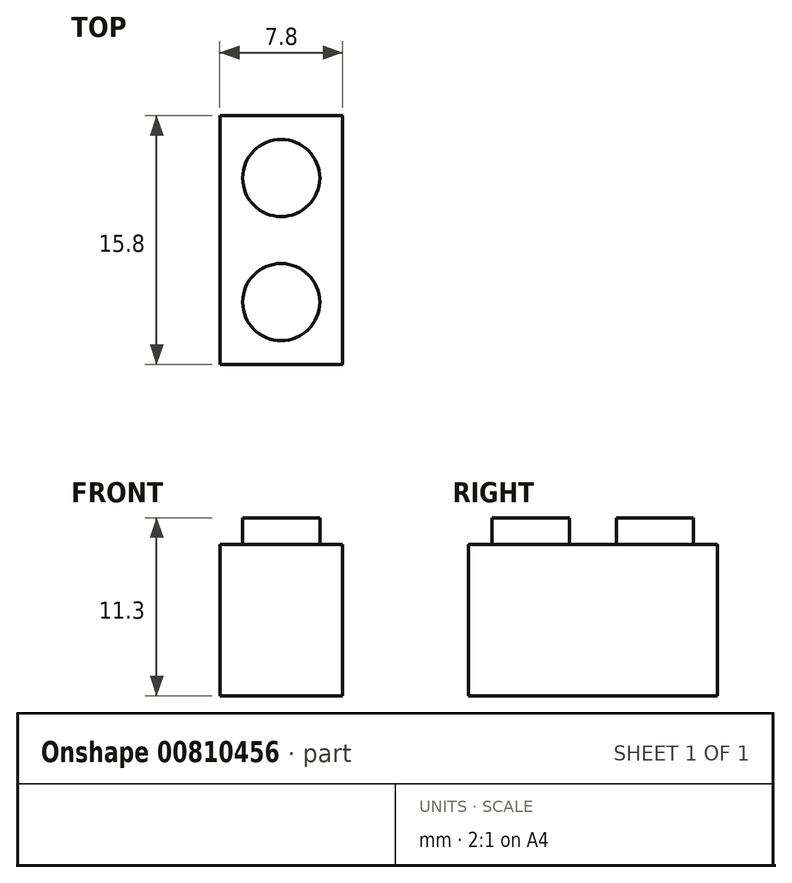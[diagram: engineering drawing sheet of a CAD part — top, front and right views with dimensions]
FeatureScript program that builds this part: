
annotation { "Feature Type Name" : "Feature", "Feature Type Description" : "" }
export const myFeature = defineFeature(function(context is Context, id is Id, definition is map)
    precondition{}
    {
        {
            var Q0;
            Q0=qCreatedBy(makeId("Top.planeOp"),FACE);
            var sketch = newSketch(context, id + "F0", { "sketchPlane" : qUnion([Q0])});
            skLineSegment(sketch, "E0", {"start": v(-4.58, 12.27) * mm, "end": v(-4.58, -3.53) * mm});
            skLineSegment(sketch, "E1", {"start": v(-4.58, -3.53) * mm, "end": v(3.22, -3.53) * mm});
            skLineSegment(sketch, "E2", {"start": v(3.22, -3.53) * mm, "end": v(3.22, 12.27) * mm});
            skLineSegment(sketch, "E3", {"start": v(3.22, 12.27) * mm, "end": v(-4.58, 12.27) * mm});
            skSolve(sketch);
        }
        {
            var Q0;
            Q0=makeQuery(id+"F0.imprint","IMPRINT",FACE,{"disambiguationData":[TD([[makeQuery(id+"F0.imprint","IMPRINT",EDGE,{"derivedFrom":sQuery(id+"F0.wireOp",EDGE,"E0")}),1.0]])]});
            extrude(context, id + "F1", {"entities" : qUnion([Q0]), "depth" : 9.6 * mm, "offsetDistance" : 25.4 * mm});
        }
        {
            var Q0;
            Q0=makeQuery(id+"F1.opExtrude","CAP_FACE",FACE,{"disambiguationData":[OSD([sQuery(id+"F0.wireOp",EDGE,"E0"),sQuery(id+"F0.wireOp",EDGE,"E1"),sQuery(id+"F0.wireOp",EDGE,"E2"),sQuery(id+"F0.wireOp",EDGE,"E3")])],"isStart":false});
            var sketch = newSketch(context, id + "F2", { "sketchPlane" : qUnion([Q0])});
            skLineSegment(sketch, "E4", {"start": v(-4.58, -3.53) * mm, "end": v(-0.68, -3.53) * mm, "construction": true});
            skLineSegment(sketch, "E5", {"start": v(-0.68, -3.53) * mm, "end": v(-0.68, 0.43) * mm, "construction": true});
            skCircle(sketch, "E6", {"center": v(-0.68, 0.43) * mm, "radius": 2.45 * mm});
            skLineSegment(sketch, "E7", {"start": v(-0.68, 12.27) * mm, "end": v(-0.68, 8.31) * mm, "construction": true});
            skCircle(sketch, "E8", {"center": v(-0.68, 8.31) * mm, "radius": 2.45 * mm});
            skSolve(sketch);
        }
        {
            var Q0;
            Q0=makeQuery(id+"F2.imprint","IMPRINT",FACE,{"disambiguationData":[TD([[makeQuery(id+"F2.imprint","IMPRINT",EDGE,{"derivedFrom":sQuery(id+"F2.wireOp",EDGE,"E6")}),1.0]])]});
            var Q1;
            Q1=makeQuery(id+"F2.imprint","IMPRINT",FACE,{"disambiguationData":[TD([[makeQuery(id+"F2.imprint","IMPRINT",EDGE,{"derivedFrom":sQuery(id+"F2.wireOp",EDGE,"E8")}),1.0]])]});
            extrude(context, id + "F3", {"entities" : qUnion([Q0, Q1]), "operationType" : NewBodyOperationType.ADD, "depth" : 1.7 * mm, "offsetDistance" : 25.4 * mm});
        }
    });
